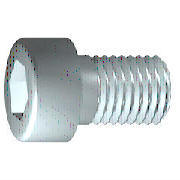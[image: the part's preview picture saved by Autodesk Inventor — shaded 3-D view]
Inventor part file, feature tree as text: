
AUTODESK INVENTOR PART (.ipt)
format: ipt  version: 2024 (Build 280153000, 153)  size: 190,976 bytes
history: native  units: mm (DEFAULTED — no unit token found)
features: fillet x2, sketch x2, extrude x1, thread x1, chamfer x1, plane x1
ambient origin geometry x7: Origin, YZ Plane, XY Plane, X Axis, Y Axis, Z Axis, Center Point
bodies: Solid1 (feature_tree), Body (feature_tree)
feature tree (8):
  extrude  "Slot"  Depth=3.0mm
  fillet  "Fillet1"  Radius=3.0mm
  thread  "Thread"  [1 undecoded]
  chamfer  "Chamfer1"  Distance=3.0mm
  plane  "Work Plane1"
  fillet  "Fillet2"  Radius=3.0mm
  sketch  "Sketch1"  dims[d1=10.75mm d2=0.306825mm d3=3.0mm d4=1.3mm]
  sketch  "Sketch2"  dims[d5=60.0deg d6=3.0mm d7=3.0mm d8=2.886751mm d9=5.5mm d10=90.0deg d11=10.0mm d12=0.0mm d13=10.75mm d14=0.0mm d15=0.306725mm d16=0.306725mm d17=0.3mm d19=0.0mm d26=12.0mm d27=45.0deg d28=0.0mm d29=0.0mm d30=0.1mm]
note: 1 required parameter value undecoded (feature->parameter linkage not recoverable at this tier; creation-order binding heuristic only, values carry confidence <= 0.55)
